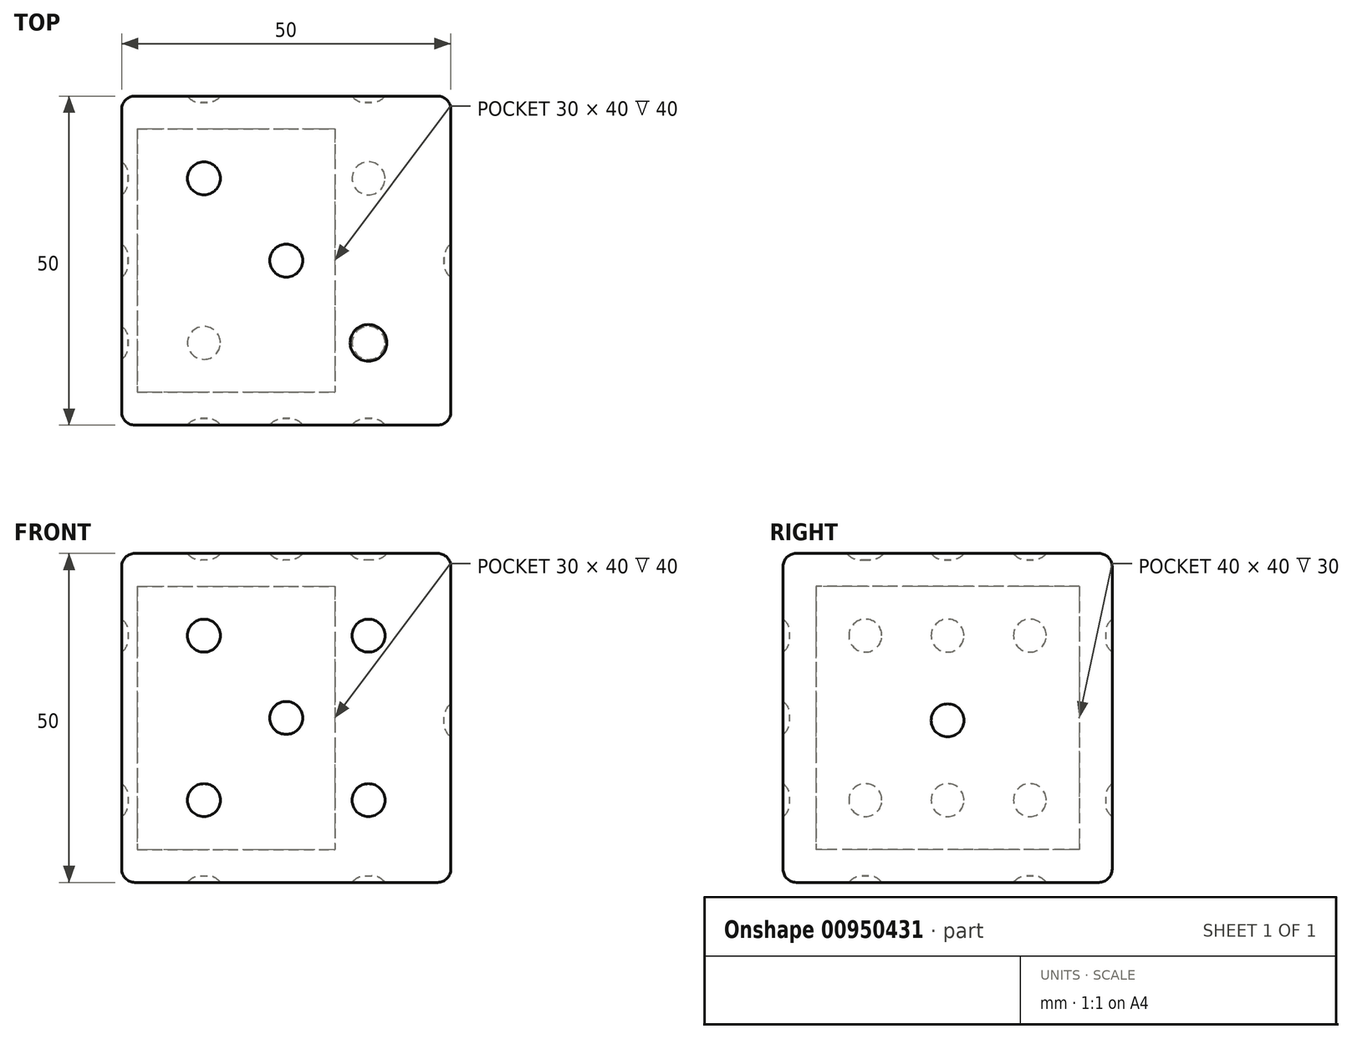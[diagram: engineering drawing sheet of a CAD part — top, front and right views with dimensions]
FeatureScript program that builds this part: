
annotation { "Feature Type Name" : "Feature", "Feature Type Description" : "" }
export const myFeature = defineFeature(function(context is Context, id is Id, definition is map)
    precondition{}
    {
        {
            var Q0;
            Q0=qCreatedBy(makeId("Top.planeOp"),FACE);
            var sketch = newSketch(context, id + "F0", { "sketchPlane" : qUnion([Q0])});
            skLineSegment(sketch, "E0.bottom", {"start": v(25, 25) * mm, "end": v(-25, 25) * mm});
            skLineSegment(sketch, "E0.top", {"start": v(25, -25) * mm, "end": v(-25, -25) * mm});
            skLineSegment(sketch, "E0.left", {"start": v(25, 25) * mm, "end": v(25, -25) * mm});
            skLineSegment(sketch, "E0.right", {"start": v(-25, 25) * mm, "end": v(-25, -25) * mm});
            skPoint(sketch, "E0.middle", {"position": v(0, 0) * mm});
            skSolve(sketch);
        }
        {
            var Q0;
            Q0 = qSketchRegion(id + "F0", true);
            extrude(context, id + "F1", {"entities" : qUnion([Q0]), "depth" : 50 * mm, "offsetDistance" : 25 * mm});
        }
        {
            var Q0;
            Q0=makeQuery(id+"F1.opExtrude","CAP_FACE",FACE,{"disambiguationData":[OSD([sQuery(id+"F0.wireOp",EDGE,"E0.bottom"),sQuery(id+"F0.wireOp",EDGE,"E0.top"),sQuery(id+"F0.wireOp",EDGE,"E0.left"),sQuery(id+"F0.wireOp",EDGE,"E0.right")])],"isStart":false});
            var sketch = newSketch(context, id + "F2", { "sketchPlane" : qUnion([Q0])});
            skLineSegment(sketch, "E1", {"start": v(0, 25) * mm, "end": v(0, -25) * mm, "construction": true});
            skLineSegment(sketch, "E2", {"start": v(-25, 0) * mm, "end": v(25, 0) * mm, "construction": true});
            skLineSegment(sketch, "E3", {"start": v(0, 12.5) * mm, "end": v(25, 12.5) * mm, "construction": true});
            skLineSegment(sketch, "E4", {"start": v(-12.5, 0) * mm, "end": v(-12.5, -25) * mm, "construction": true});
            skLineSegment(sketch, "E5", {"start": v(-12.5, -25) * mm, "end": v(-12.5, 25) * mm, "construction": true});
            skLineSegment(sketch, "E6", {"start": v(0, 12.5) * mm, "end": v(-25, 12.5) * mm, "construction": true});
            skLineSegment(sketch, "E7", {"start": v(-25, 12.5) * mm, "end": v(-25, -25) * mm, "construction": true});
            skLineSegment(sketch, "E8", {"start": v(0, -12.5) * mm, "end": v(25, -12.5) * mm, "construction": true});
            skLineSegment(sketch, "E9", {"start": v(25, -12.5) * mm, "end": v(-25, -12.5) * mm, "construction": true});
            skLineSegment(sketch, "E10", {"start": v(12.5, 0) * mm, "end": v(12.5, -25) * mm, "construction": true});
            skLineSegment(sketch, "E11", {"start": v(12.5, -25) * mm, "end": v(12.5, 25) * mm, "construction": true});
            skCircle(sketch, "E12", {"center": v(12.5, -12.5) * mm, "radius": 2.79 * mm});
            skCircle(sketch, "E13", {"center": v(0, 0) * mm, "radius": 2.5 * mm});
            skCircle(sketch, "E14", {"center": v(-12.5, 12.5) * mm, "radius": 2.5 * mm});
            skSolve(sketch);
        }
        {
            var Q0;
            Q0=makeQuery(id+"F1.opExtrude","SWEPT_FACE",FACE,{"disambiguationData":[OSD([sQuery(id+"F0.wireOp",EDGE,"E0.right")])]});
            var sketch = newSketch(context, id + "F3", { "sketchPlane" : qUnion([Q0])});
            skLineSegment(sketch, "E15", {"start": v(0, 0) * mm, "end": v(0, 50) * mm, "construction": true});
            skLineSegment(sketch, "E16", {"start": v(25, 25) * mm, "end": v(-25, 25) * mm, "construction": true});
            skLineSegment(sketch, "E17", {"start": v(12.5, 25) * mm, "end": v(12.5, 50) * mm, "construction": true});
            skLineSegment(sketch, "E18", {"start": v(12.5, 50) * mm, "end": v(12.5, 0) * mm, "construction": true});
            skLineSegment(sketch, "E19", {"start": v(0, 37.5) * mm, "end": v(-25, 37.5) * mm, "construction": true});
            skLineSegment(sketch, "E20", {"start": v(-25, 37.5) * mm, "end": v(25, 37.5) * mm, "construction": true});
            skLineSegment(sketch, "E21", {"start": v(-12.5, 25) * mm, "end": v(-12.5, 0) * mm, "construction": true});
            skLineSegment(sketch, "E22", {"start": v(-12.5, 0) * mm, "end": v(-12.5, 50) * mm, "construction": true});
            skLineSegment(sketch, "E23", {"start": v(0, 12.5) * mm, "end": v(-25, 12.5) * mm, "construction": true});
            skLineSegment(sketch, "E24", {"start": v(-25, 12.5) * mm, "end": v(25, 12.5) * mm, "construction": true});
            skCircle(sketch, "E25", {"center": v(-12.5, 12.5) * mm, "radius": 2.5 * mm});
            skCircle(sketch, "E26", {"center": v(-12.5, 37.5) * mm, "radius": 2.5 * mm});
            skCircle(sketch, "E27", {"center": v(0, 37.5) * mm, "radius": 2.5 * mm});
            skCircle(sketch, "E28", {"center": v(12.5, 37.5) * mm, "radius": 2.5 * mm});
            skCircle(sketch, "E29", {"center": v(12.5, 12.5) * mm, "radius": 2.5 * mm});
            skCircle(sketch, "E30", {"center": v(0, 12.5) * mm, "radius": 2.5 * mm});
            skSolve(sketch);
        }
        {
            var Q0;
            Q0=makeQuery(id+"F1.opExtrude","SWEPT_FACE",FACE,{"disambiguationData":[OSD([sQuery(id+"F0.wireOp",EDGE,"E0.top")])]});
            var sketch = newSketch(context, id + "F4", { "sketchPlane" : qUnion([Q0])});
            skLineSegment(sketch, "E31", {"start": v(0, 0) * mm, "end": v(0, 50) * mm, "construction": true});
            skLineSegment(sketch, "E32", {"start": v(0, 25) * mm, "end": v(25, 25) * mm, "construction": true});
            skLineSegment(sketch, "E33", {"start": v(25, 25) * mm, "end": v(-25, 25) * mm, "construction": true});
            skLineSegment(sketch, "E34", {"start": v(-12.5, 37.5) * mm, "end": v(25, 37.5) * mm, "construction": true});
            skLineSegment(sketch, "E35", {"start": v(12.5, 25) * mm, "end": v(12.5, 0) * mm, "construction": true});
            skLineSegment(sketch, "E36", {"start": v(12.5, 0) * mm, "end": v(12.5, 50) * mm, "construction": true});
            skLineSegment(sketch, "E37", {"start": v(-25, 37.5) * mm, "end": v(25, 37.5) * mm, "construction": true});
            skLineSegment(sketch, "E38", {"start": v(-12.5, 12.5) * mm, "end": v(-12.5, 50) * mm, "construction": true});
            skLineSegment(sketch, "E39", {"start": v(-12.5, 50) * mm, "end": v(-12.5, 0) * mm, "construction": true});
            skLineSegment(sketch, "E40", {"start": v(-12.5, 0) * mm, "end": v(-12.5, 12.5) * mm, "construction": true});
            skLineSegment(sketch, "E41", {"start": v(-12.5, 12.5) * mm, "end": v(-25, 12.5) * mm, "construction": true});
            skLineSegment(sketch, "E42", {"start": v(-25, 12.5) * mm, "end": v(25, 12.5) * mm, "construction": true});
            skCircle(sketch, "E43", {"center": v(-12.5, 37.5) * mm, "radius": 2.5 * mm});
            skCircle(sketch, "E44", {"center": v(12.5, 12.5) * mm, "radius": 2.5 * mm});
            skCircle(sketch, "E45", {"center": v(12.5, 37.5) * mm, "radius": 2.5 * mm});
            skCircle(sketch, "E46", {"center": v(0, 25) * mm, "radius": 2.5 * mm});
            skCircle(sketch, "E47", {"center": v(-12.5, 12.5) * mm, "radius": 2.5 * mm});
            skSolve(sketch);
        }
        {
            var Q0;
            Q0=makeQuery(id+"F1.opExtrude","SWEPT_FACE",FACE,{"disambiguationData":[OSD([sQuery(id+"F0.wireOp",EDGE,"E0.left")])]});
            var sketch = newSketch(context, id + "F5", { "sketchPlane" : qUnion([Q0])});
            skCircle(sketch, "E48", {"center": v(0, 24.63) * mm, "radius": 2.5 * mm});
            skSolve(sketch);
        }
        {
            var Q0;
            Q0=makeQuery(id+"F3.imprint","IMPRINT",FACE,{"disambiguationData":[TD([[makeQuery(id+"F3.imprint","IMPRINT",EDGE,{"derivedFrom":sQuery(id+"F3.wireOp",EDGE,"E27")}),1.0]])]});
            var Q1;
            Q1=makeQuery(id+"F3.imprint","IMPRINT",FACE,{"disambiguationData":[TD([[makeQuery(id+"F3.imprint","IMPRINT",EDGE,{"derivedFrom":sQuery(id+"F3.wireOp",EDGE,"E28")}),1.0]])]});
            var Q2;
            Q2=makeQuery(id+"F3.imprint","IMPRINT",FACE,{"disambiguationData":[TD([[makeQuery(id+"F3.imprint","IMPRINT",EDGE,{"derivedFrom":sQuery(id+"F3.wireOp",EDGE,"E29")}),1.0]])]});
            var Q3;
            Q3=makeQuery(id+"F3.imprint","IMPRINT",FACE,{"disambiguationData":[TD([[makeQuery(id+"F3.imprint","IMPRINT",EDGE,{"derivedFrom":sQuery(id+"F3.wireOp",EDGE,"E30")}),1.0]])]});
            var Q4;
            Q4=makeQuery(id+"F3.imprint","IMPRINT",FACE,{"disambiguationData":[TD([[makeQuery(id+"F3.imprint","IMPRINT",EDGE,{"derivedFrom":sQuery(id+"F3.wireOp",EDGE,"E25")}),1.0]])]});
            var Q5;
            Q5=makeQuery(id+"F3.imprint","IMPRINT",FACE,{"disambiguationData":[TD([[makeQuery(id+"F3.imprint","IMPRINT",EDGE,{"derivedFrom":sQuery(id+"F3.wireOp",EDGE,"E26")}),1.0]])]});
            extrude(context, id + "F6", {"entities" : qUnion([Q0, Q1, Q2, Q3, Q4, Q5]), "operationType" : NewBodyOperationType.REMOVE, "oppositeDirection" : true, "depth" : 1 * mm, "offsetDistance" : 25 * mm});
        }
        {
            var Q0;
            Q0 = qSketchRegion(id + "F5", true);
            extrude(context, id + "F7", {"entities" : qUnion([Q0]), "operationType" : NewBodyOperationType.REMOVE, "oppositeDirection" : true, "depth" : 1 * mm, "offsetDistance" : 25 * mm});
        }
        {
            var Q0;
            Q0 = qSketchRegion(id + "F2", true);
            extrude(context, id + "F8", {"entities" : qUnion([Q0]), "operationType" : NewBodyOperationType.REMOVE, "oppositeDirection" : true, "depth" : 1 * mm, "offsetDistance" : 25 * mm});
        }
        {
            var Q0;
            Q0=makeQuery(id+"F1.opExtrude","CAP_FACE",FACE,{"disambiguationData":[OSD([sQuery(id+"F0.wireOp",EDGE,"E0.bottom"),sQuery(id+"F0.wireOp",EDGE,"E0.top"),sQuery(id+"F0.wireOp",EDGE,"E0.left"),sQuery(id+"F0.wireOp",EDGE,"E0.right")])],"isStart":true});
            var sketch = newSketch(context, id + "F9", { "sketchPlane" : qUnion([Q0])});
            skPoint(sketch, "E49.endSnap0", {"position": v(-12.5, 12.5) * mm});
            skPoint(sketch, "E50.endSnap0", {"position": v(12.5, 12.5) * mm});
            skPoint(sketch, "E51.endSnap0", {"position": v(-12.5, -12.5) * mm});
            skLineSegment(sketch, "E52.bottom", {"start": v(-12.5, -12.5) * mm, "end": v(12.5, -12.5) * mm, "construction": true});
            skLineSegment(sketch, "E52.top", {"start": v(-12.5, 12.5) * mm, "end": v(12.5, 12.5) * mm, "construction": true});
            skLineSegment(sketch, "E52.left", {"start": v(-12.5, -12.5) * mm, "end": v(-12.5, 12.5) * mm, "construction": true});
            skLineSegment(sketch, "E52.right", {"start": v(12.5, -12.5) * mm, "end": v(12.5, 12.5) * mm, "construction": true});
            skLineSegment(sketch, "E53.left", {"start": v(6.9, 18.1) * mm, "end": v(6.9, 19.7) * mm, "construction": true});
            skLineSegment(sketch, "E53.right", {"start": v(-10, 18.1) * mm, "end": v(-10, 19.7) * mm, "construction": true});
            skCircle(sketch, "E54", {"center": v(12.5, 12.5) * mm, "radius": 2.5 * mm});
            skCircle(sketch, "E55", {"center": v(12.5, -12.5) * mm, "radius": 2.5 * mm});
            skCircle(sketch, "E56", {"center": v(-12.5, -12.5) * mm, "radius": 2.5 * mm});
            skCircle(sketch, "E57", {"center": v(-12.5, 12.5) * mm, "radius": 2.5 * mm});
            skSolve(sketch);
        }
        {
            var Q0;
            Q0 = qSketchRegion(id + "F9", true);
            extrude(context, id + "F10", {"entities" : qUnion([Q0]), "operationType" : NewBodyOperationType.REMOVE, "oppositeDirection" : true, "depth" : 1 * mm, "offsetDistance" : 25 * mm});
        }
        {
            var Q0;
            Q0 = qSketchRegion(id + "F4", true);
            extrude(context, id + "F11", {"entities" : qUnion([Q0]), "operationType" : NewBodyOperationType.REMOVE, "oppositeDirection" : true, "depth" : 1 * mm, "offsetDistance" : 25 * mm});
        }
        {
            var Q0;
            Q0=makeQuery(id+"F1.opExtrude","SWEPT_FACE",FACE,{"disambiguationData":[OSD([sQuery(id+"F0.wireOp",EDGE,"E0.bottom")])]});
            var sketch = newSketch(context, id + "F12", { "sketchPlane" : qUnion([Q0])});
            skLineSegment(sketch, "E58", {"start": v(-25, 50) * mm, "end": v(25, 0) * mm, "construction": true});
            skLineSegment(sketch, "E59", {"start": v(25, 0) * mm, "end": v(25, 50) * mm, "construction": true});
            skLineSegment(sketch, "E60", {"start": v(25, 50) * mm, "end": v(0, 0) * mm, "construction": true});
            skLineSegment(sketch, "E61", {"start": v(0, 50) * mm, "end": v(-25, 0) * mm, "construction": true});
            skLineSegment(sketch, "E62", {"start": v(0, 25) * mm, "end": v(25, 25) * mm, "construction": true});
            skLineSegment(sketch, "E63", {"start": v(-25, 25) * mm, "end": v(0, 25) * mm, "construction": true});
            skLineSegment(sketch, "E64", {"start": v(0, 0) * mm, "end": v(0, 50) * mm, "construction": true});
            skLineSegment(sketch, "E65", {"start": v(-25, 0) * mm, "end": v(25, 25) * mm, "construction": true});
            skLineSegment(sketch, "E66", {"start": v(25, 25) * mm, "end": v(-25, 50) * mm, "construction": true});
            skLineSegment(sketch, "E67", {"start": v(12.5, 25) * mm, "end": v(12.5, 0) * mm, "construction": true});
            skLineSegment(sketch, "E68", {"start": v(12.5, 0) * mm, "end": v(-12.5, 25) * mm, "construction": true});
            skLineSegment(sketch, "E69", {"start": v(-12.5, 25) * mm, "end": v(-12.5, 50) * mm, "construction": true});
            skCircle(sketch, "E70", {"center": v(-12.5, 37.5) * mm, "radius": 2.5 * mm});
            skCircle(sketch, "E71", {"center": v(12.5, 12.5) * mm, "radius": 2.5 * mm});
            skSolve(sketch);
        }
        {
            var Q0;
            Q0 = qSketchRegion(id + "F12", true);
            extrude(context, id + "F13", {"entities" : qUnion([Q0]), "operationType" : NewBodyOperationType.REMOVE, "oppositeDirection" : true, "depth" : 1 * mm, "offsetDistance" : 25 * mm});
        }
        {
            var Q0;
            Q0=makeQuery(id+"F1.opExtrude","SWEPT_FACE",FACE,{"disambiguationData":[OSD([sQuery(id+"F0.wireOp",EDGE,"E0.top")])]});
            var sketch = newSketch(context, id + "F14", { "sketchPlane" : qUnion([Q0])});
            skLineSegment(sketch, "E72.bottom", {"start": v(7.38, 50) * mm, "end": v(25, 50) * mm});
            skLineSegment(sketch, "E72.top", {"start": v(7.38, 0) * mm, "end": v(25, 0) * mm});
            skLineSegment(sketch, "E72.left", {"start": v(7.38, 50) * mm, "end": v(7.38, 0) * mm});
            skLineSegment(sketch, "E72.right", {"start": v(25, 50) * mm, "end": v(25, 0) * mm});
            skSolve(sketch);
        }
        {
            var Q0;
            Q0=sQuery(id+"F14.wireOp",EDGE,"E72.left");
            cPlane(context, id + "F15", {"entities" : qUnion([Q0]), "cplaneType" : CPlaneType.LINE_ANGLE, "offset" : 25 * mm, "angle" : 0 * degree, "width" : 150 * mm, "height" : 150 * mm});
        }
        {
            var Q0;
            Q0=qCreatedBy(id+"F15.planeOp",FACE);
            var sketch = newSketch(context, id + "F16", { "sketchPlane" : qUnion([Q0])});
            skLineSegment(sketch, "E73.0", {"start": v(-20, 45) * mm, "end": v(20, 45) * mm});
            skLineSegment(sketch, "E73.1", {"start": v(-20, 45) * mm, "end": v(-20, 5) * mm});
            skLineSegment(sketch, "E73.2", {"start": v(-20, 5) * mm, "end": v(20, 5) * mm});
            skLineSegment(sketch, "E73.3", {"start": v(20, 45) * mm, "end": v(20, 5) * mm});
            skSolve(sketch);
        }
        {
            var Q0;
            Q0 = qSketchRegion(id + "F16", true);
            extrude(context, id + "F17", {"entities" : qUnion([Q0]), "operationType" : NewBodyOperationType.REMOVE, "depth" : 30 * mm, "offsetDistance" : 25 * mm});
        }
        {
            var Q0;
            Q0 = qSketchRegion(id + "F16", true);
            extrude(context, id + "F18", {"entities" : qUnion([Q0]), "depth" : 30 * mm, "offsetDistance" : 25 * mm});
        }
        {
            var Q0;
            Q0=makeQuery(id+"F1.opExtrude","CAP_EDGE",EDGE,{"disambiguationData":[OSD([sQuery(id+"F0.wireOp",EDGE,"E0.right")])],"isStart":false});
            var Q1;
            Q1=makeQuery(id+"F1.opExtrude","SWEPT_EDGE",EDGE,{"disambiguationData":[OSD([sQuery(id+"F0.wireOp",EDGE,"E0.bottom"),sQuery(id+"F0.wireOp",EDGE,"E0.right")])]});
            var Q2;
            Q2=makeQuery(id+"F1.opExtrude","CAP_EDGE",EDGE,{"disambiguationData":[OSD([sQuery(id+"F0.wireOp",EDGE,"E0.right")])],"isStart":true});
            var Q3;
            Q3=makeQuery(id+"F1.opExtrude","SWEPT_EDGE",EDGE,{"disambiguationData":[OSD([sQuery(id+"F0.wireOp",EDGE,"E0.top"),sQuery(id+"F0.wireOp",EDGE,"E0.right")])]});
            var Q4;
            Q4=makeQuery(id+"F1.opExtrude","CAP_EDGE",EDGE,{"disambiguationData":[OSD([sQuery(id+"F0.wireOp",EDGE,"E0.top")])],"isStart":false});
            var Q5;
            Q5=makeQuery(id+"F1.opExtrude","CAP_EDGE",EDGE,{"disambiguationData":[OSD([sQuery(id+"F0.wireOp",EDGE,"E0.left")])],"isStart":false});
            var Q6;
            Q6=makeQuery(id+"F1.opExtrude","CAP_EDGE",EDGE,{"disambiguationData":[OSD([sQuery(id+"F0.wireOp",EDGE,"E0.bottom")])],"isStart":false});
            var Q7;
            Q7=makeQuery(id+"F1.opExtrude","CAP_EDGE",EDGE,{"disambiguationData":[OSD([sQuery(id+"F0.wireOp",EDGE,"E0.top")])],"isStart":true});
            var Q8;
            Q8=makeQuery(id+"F1.opExtrude","CAP_EDGE",EDGE,{"disambiguationData":[OSD([sQuery(id+"F0.wireOp",EDGE,"E0.left")])],"isStart":true});
            var Q9;
            Q9=makeQuery(id+"F1.opExtrude","CAP_EDGE",EDGE,{"disambiguationData":[OSD([sQuery(id+"F0.wireOp",EDGE,"E0.bottom")])],"isStart":true});
            var Q10;
            Q10=makeQuery(id+"F1.opExtrude","SWEPT_EDGE",EDGE,{"disambiguationData":[OSD([sQuery(id+"F0.wireOp",EDGE,"E0.bottom"),sQuery(id+"F0.wireOp",EDGE,"E0.left")])]});
            var Q11;
            Q11=makeQuery(id+"F1.opExtrude","SWEPT_EDGE",EDGE,{"disambiguationData":[OSD([sQuery(id+"F0.wireOp",EDGE,"E0.top"),sQuery(id+"F0.wireOp",EDGE,"E0.left")])]});
            fillet(context, id + "F19", {"entities" : qUnion([Q0, Q1, Q2, Q3, Q4, Q5, Q6, Q7, Q8, Q9, Q10, Q11]), "radius" : 2 * mm, "tangentPropagation" : true, "allowEdgeOverflow" : false});
        }
        {
            var Q0;
            Q0=makeQuery(id+"F8.boolean.opBoolean","COPY",FACE,{"derivedFrom":makeQuery(id+"F8.opExtrude","CAP_FACE",FACE,{"disambiguationData":[OSD([sQuery(id+"F2.wireOp",EDGE,"E14")])],"isStart":false})});
            var Q1;
            Q1=makeQuery(id+"F8.boolean.opBoolean","COPY",FACE,{"derivedFrom":makeQuery(id+"F8.opExtrude","CAP_FACE",FACE,{"disambiguationData":[OSD([sQuery(id+"F2.wireOp",EDGE,"E12")])],"isStart":false})});
            var Q2;
            Q2=makeQuery(id+"F8.boolean.opBoolean","COPY",FACE,{"derivedFrom":makeQuery(id+"F8.opExtrude","CAP_FACE",FACE,{"disambiguationData":[OSD([sQuery(id+"F2.wireOp",EDGE,"E13")])],"isStart":false})});
            var Q3;
            Q3=makeQuery(id+"F8.boolean.opBoolean","COPY",FACE,{"derivedFrom":makeQuery(id+"F8.opExtrude","CAP_FACE",FACE,{"disambiguationData":[OSD([sQuery(id+"F2.wireOp",EDGE,"E14")])],"isStart":false})});
            var Q4;
            Q4=makeQuery(id+"F13.boolean.opBoolean","COPY",FACE,{"derivedFrom":makeQuery(id+"F13.opExtrude","CAP_FACE",FACE,{"disambiguationData":[OSD([sQuery(id+"F12.wireOp",EDGE,"E70")])],"isStart":false})});
            var Q5;
            Q5=makeQuery(id+"F13.boolean.opBoolean","COPY",FACE,{"derivedFrom":makeQuery(id+"F13.opExtrude","CAP_FACE",FACE,{"disambiguationData":[OSD([sQuery(id+"F12.wireOp",EDGE,"E71")])],"isStart":false})});
            var Q6;
            Q6=makeQuery(id+"F8.boolean.opBoolean","COPY",EDGE,{"derivedFrom":makeQuery(id+"F8.opExtrude","CAP_EDGE",EDGE,{"disambiguationData":[OSD([sQuery(id+"F2.wireOp",EDGE,"E13")])],"isStart":false})});
            var Q7;
            Q7=makeQuery(id+"F8.boolean.opBoolean","COPY",EDGE,{"derivedFrom":makeQuery(id+"F8.opExtrude","CAP_EDGE",EDGE,{"disambiguationData":[OSD([sQuery(id+"F2.wireOp",EDGE,"E12")])],"isStart":false})});
            var Q8;
            Q8=makeQuery(id+"F6.boolean.opBoolean","COPY",FACE,{"derivedFrom":makeQuery(id+"F6.opExtrude","CAP_FACE",FACE,{"disambiguationData":[OSD([sQuery(id+"F3.wireOp",EDGE,"E26")])],"isStart":false})});
            var Q9;
            Q9=makeQuery(id+"F6.boolean.opBoolean","COPY",FACE,{"derivedFrom":makeQuery(id+"F6.opExtrude","CAP_FACE",FACE,{"disambiguationData":[OSD([sQuery(id+"F3.wireOp",EDGE,"E30")])],"isStart":false})});
            var Q10;
            Q10=makeQuery(id+"F6.boolean.opBoolean","COPY",FACE,{"derivedFrom":makeQuery(id+"F6.opExtrude","CAP_FACE",FACE,{"disambiguationData":[OSD([sQuery(id+"F3.wireOp",EDGE,"E25")])],"isStart":false})});
            var Q11;
            Q11=makeQuery(id+"F6.boolean.opBoolean","COPY",EDGE,{"derivedFrom":makeQuery(id+"F6.opExtrude","CAP_EDGE",EDGE,{"disambiguationData":[OSD([sQuery(id+"F3.wireOp",EDGE,"E27")])],"isStart":false})});
            var Q12;
            Q12=makeQuery(id+"F6.boolean.opBoolean","COPY",FACE,{"derivedFrom":makeQuery(id+"F6.opExtrude","CAP_FACE",FACE,{"disambiguationData":[OSD([sQuery(id+"F3.wireOp",EDGE,"E28")])],"isStart":false})});
            var Q13;
            Q13=makeQuery(id+"F6.boolean.opBoolean","COPY",FACE,{"derivedFrom":makeQuery(id+"F6.opExtrude","CAP_FACE",FACE,{"disambiguationData":[OSD([sQuery(id+"F3.wireOp",EDGE,"E29")])],"isStart":false})});
            var Q14;
            Q14=makeQuery(id+"F10.boolean.opBoolean","COPY",EDGE,{"derivedFrom":makeQuery(id+"F10.opExtrude","CAP_EDGE",EDGE,{"disambiguationData":[OSD([sQuery(id+"F9.wireOp",EDGE,"E54")])],"isStart":false})});
            var Q15;
            Q15=makeQuery(id+"F10.boolean.opBoolean","COPY",EDGE,{"derivedFrom":makeQuery(id+"F10.opExtrude","CAP_EDGE",EDGE,{"disambiguationData":[OSD([sQuery(id+"F9.wireOp",EDGE,"E55")])],"isStart":false})});
            var Q16;
            Q16=makeQuery(id+"F11.boolean.opBoolean","COPY",EDGE,{"derivedFrom":makeQuery(id+"F11.opExtrude","CAP_EDGE",EDGE,{"disambiguationData":[OSD([sQuery(id+"F4.wireOp",EDGE,"E47")])],"isStart":false})});
            var Q17;
            Q17=makeQuery(id+"F10.boolean.opBoolean","COPY",EDGE,{"derivedFrom":makeQuery(id+"F10.opExtrude","CAP_EDGE",EDGE,{"disambiguationData":[OSD([sQuery(id+"F9.wireOp",EDGE,"E57")])],"isStart":false})});
            var Q18;
            Q18=makeQuery(id+"F10.boolean.opBoolean","COPY",EDGE,{"derivedFrom":makeQuery(id+"F10.opExtrude","CAP_EDGE",EDGE,{"disambiguationData":[OSD([sQuery(id+"F9.wireOp",EDGE,"E56")])],"isStart":false})});
            var Q19;
            Q19=makeQuery(id+"F7.boolean.opBoolean","COPY",EDGE,{"derivedFrom":makeQuery(id+"F7.opExtrude","CAP_EDGE",EDGE,{"disambiguationData":[OSD([sQuery(id+"F5.wireOp",EDGE,"E48")])],"isStart":false})});
            var Q20;
            Q20=makeQuery(id+"F11.boolean.opBoolean","COPY",FACE,{"derivedFrom":makeQuery(id+"F11.opExtrude","CAP_FACE",FACE,{"disambiguationData":[OSD([sQuery(id+"F4.wireOp",EDGE,"E46")])],"isStart":false})});
            var Q21;
            Q21=makeQuery(id+"F11.boolean.opBoolean","COPY",EDGE,{"derivedFrom":makeQuery(id+"F11.opExtrude","CAP_EDGE",EDGE,{"disambiguationData":[OSD([sQuery(id+"F4.wireOp",EDGE,"E44")])],"isStart":false})});
            var Q22;
            Q22=makeQuery(id+"F11.boolean.opBoolean","COPY",FACE,{"derivedFrom":makeQuery(id+"F11.opExtrude","CAP_FACE",FACE,{"disambiguationData":[OSD([sQuery(id+"F4.wireOp",EDGE,"E45")])],"isStart":false})});
            var Q23;
            Q23=makeQuery(id+"F11.boolean.opBoolean","COPY",FACE,{"derivedFrom":makeQuery(id+"F11.opExtrude","CAP_FACE",FACE,{"disambiguationData":[OSD([sQuery(id+"F4.wireOp",EDGE,"E43")])],"isStart":false})});
            fillet(context, id + "F20", {"entities" : qUnion([Q0, Q1, Q2, Q3, Q4, Q5, Q6, Q7, Q8, Q9, Q10, Q11, Q12, Q13, Q14, Q15, Q16, Q17, Q18, Q19, Q20, Q21, Q22, Q23]), "radius" : 2.5 * mm, "tangentPropagation" : true, "allowEdgeOverflow" : false});
        }
    });
